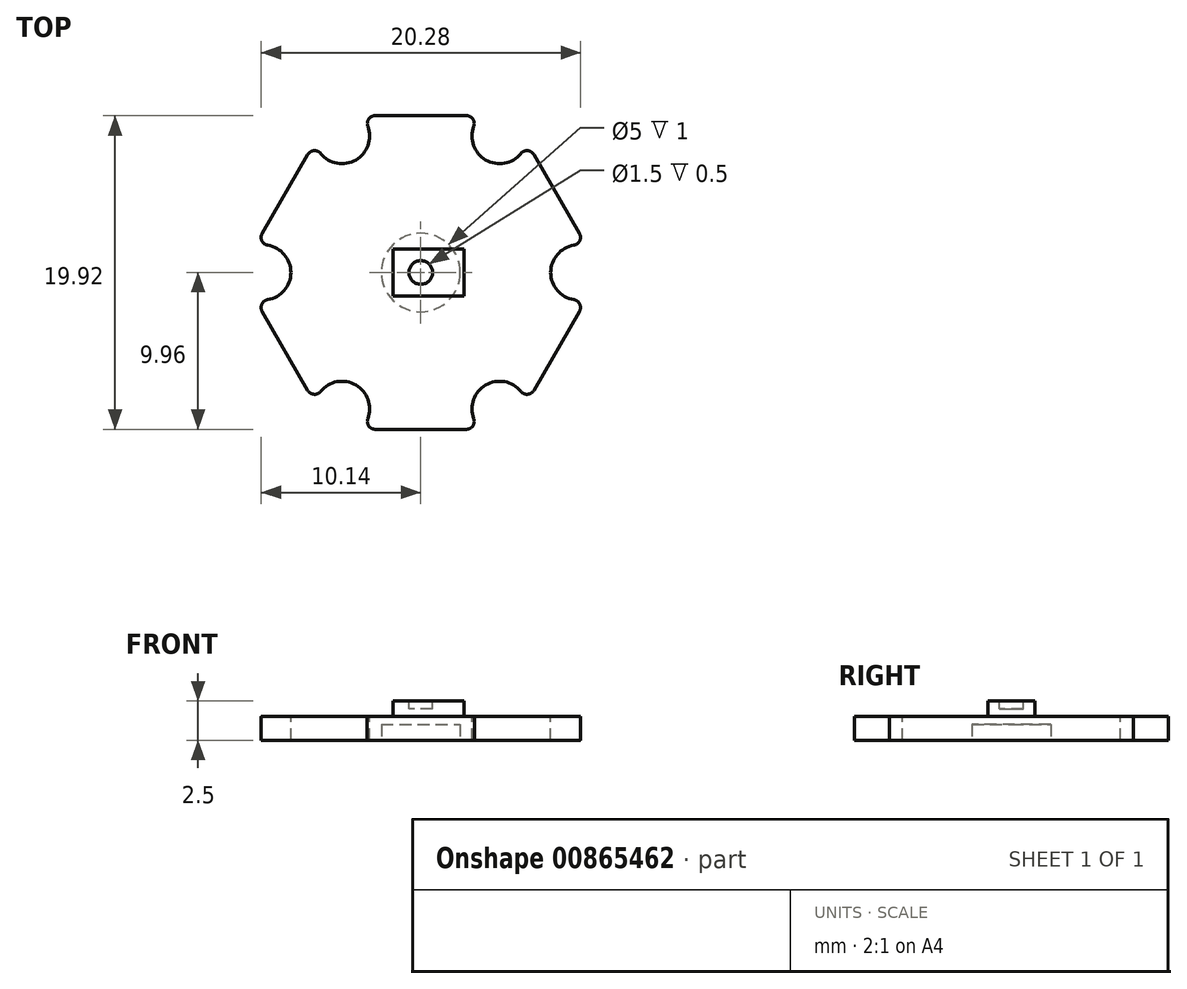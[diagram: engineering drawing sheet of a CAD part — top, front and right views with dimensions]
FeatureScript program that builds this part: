
annotation { "Feature Type Name" : "Feature", "Feature Type Description" : "" }
export const myFeature = defineFeature(function(context is Context, id is Id, definition is map)
    precondition{}
    {
        {
            var Q0;
            Q0=qCreatedBy(makeId("Top.planeOp"),FACE);
            var sketch = newSketch(context, id + "F0", { "sketchPlane" : qUnion([Q0])});
            skCircle(sketch, "E0.cCircle", {"center": v(0, 0) * mm, "radius": 9.96 * mm, "construction": true});
            skLineSegment(sketch, "E0.0", {"start": v(-5.75, 9.96) * mm, "end": v(5.75, 9.96) * mm});
            skLineSegment(sketch, "E0.1", {"start": v(5.75, 9.96) * mm, "end": v(11.5, 0) * mm});
            skLineSegment(sketch, "E0.2", {"start": v(11.5, 0) * mm, "end": v(5.75, -9.96) * mm});
            skLineSegment(sketch, "E0.3", {"start": v(5.75, -9.96) * mm, "end": v(-5.75, -9.96) * mm});
            skLineSegment(sketch, "E0.4", {"start": v(-5.75, -9.96) * mm, "end": v(-11.5, 0) * mm});
            skLineSegment(sketch, "E0.5", {"start": v(-11.5, 0) * mm, "end": v(-5.75, 9.96) * mm});
            skPoint(sketch, "E0.0.midPoint", {"position": v(0, 9.96) * mm});
            skSolve(sketch);
        }
        {
            var Q0;
            Q0 = qSketchRegion(id + "F0", true);
            extrude(context, id + "F1", {"entities" : qUnion([Q0]), "depth" : 1.5 * mm, "offsetDistance" : 25 * mm});
        }
        {
            var Q0;
            Q0=makeQuery(id+"F1.opExtrude","CAP_FACE",FACE,{"disambiguationData":[OSD([sQuery(id+"F0.wireOp",EDGE,"E0.0"),sQuery(id+"F0.wireOp",EDGE,"E0.1"),sQuery(id+"F0.wireOp",EDGE,"E0.2"),sQuery(id+"F0.wireOp",EDGE,"E0.3"),sQuery(id+"F0.wireOp",EDGE,"E0.4"),sQuery(id+"F0.wireOp",EDGE,"E0.5")])],"isStart":false});
            var sketch = newSketch(context, id + "F2", { "sketchPlane" : qUnion([Q0])});
            skLineSegment(sketch, "E1", {"start": v(-5.75, 9.96) * mm, "end": v(5.75, -9.96) * mm});
            skCircle(sketch, "E2", {"center": v(-5, 8.66) * mm, "radius": 1.75 * mm});
            skCircle(sketch, "E3", {"center": v(5, -8.66) * mm, "radius": 1.75 * mm});
            skLineSegment(sketch, "E4", {"start": v(5.75, 9.96) * mm, "end": v(-5.75, -9.96) * mm});
            skLineSegment(sketch, "E5", {"start": v(-11.5, 0) * mm, "end": v(11.5, 0) * mm});
            skCircle(sketch, "E6", {"center": v(5, 8.66) * mm, "radius": 1.75 * mm});
            skCircle(sketch, "E7", {"center": v(-5, -8.66) * mm, "radius": 1.75 * mm});
            skCircle(sketch, "E8", {"center": v(10, 0) * mm, "radius": 1.75 * mm});
            skCircle(sketch, "E9", {"center": v(-10, 0) * mm, "radius": 1.75 * mm});
            skSolve(sketch);
        }
        {
            var Q0;
            Q0 = qSketchRegion(id + "F2", true);
            extrude(context, id + "F3", {"entities" : qUnion([Q0]), "operationType" : NewBodyOperationType.REMOVE, "oppositeDirection" : true, "depth" : 25 * mm, "offsetDistance" : 25 * mm});
        }
        {
            var Q0;
            Q0=makeQuery(id+"F3.boolean.opBoolean","INTERSECT",EDGE,{"derivedFrom":[makeQuery(id+"F1.opExtrude","SWEPT_FACE",FACE,{"disambiguationData":[OSD([sQuery(id+"F0.wireOp",EDGE,"E0.0")])]}),makeQuery(id+"F3.opExtrude","SWEPT_FACE",FACE,{"disambiguationData":[OSD([sQuery(id+"F2.wireOp",EDGE,"E2")])]})]});
            var Q1;
            Q1=makeQuery(id+"F3.boolean.opBoolean","INTERSECT",EDGE,{"derivedFrom":[makeQuery(id+"F1.opExtrude","SWEPT_FACE",FACE,{"disambiguationData":[OSD([sQuery(id+"F0.wireOp",EDGE,"E0.5")])]}),makeQuery(id+"F3.opExtrude","SWEPT_FACE",FACE,{"disambiguationData":[OSD([sQuery(id+"F2.wireOp",EDGE,"E2")])]})]});
            var Q2;
            Q2=makeQuery(id+"F3.boolean.opBoolean","INTERSECT",EDGE,{"derivedFrom":[makeQuery(id+"F1.opExtrude","SWEPT_FACE",FACE,{"disambiguationData":[OSD([sQuery(id+"F0.wireOp",EDGE,"E0.0")])]}),makeQuery(id+"F3.opExtrude","SWEPT_FACE",FACE,{"disambiguationData":[OSD([sQuery(id+"F2.wireOp",EDGE,"E6")])]})]});
            var Q3;
            Q3=makeQuery(id+"F3.boolean.opBoolean","INTERSECT",EDGE,{"derivedFrom":[makeQuery(id+"F1.opExtrude","SWEPT_FACE",FACE,{"disambiguationData":[OSD([sQuery(id+"F0.wireOp",EDGE,"E0.1")])]}),makeQuery(id+"F3.opExtrude","SWEPT_FACE",FACE,{"disambiguationData":[OSD([sQuery(id+"F2.wireOp",EDGE,"E6")])]})]});
            var Q4;
            Q4=makeQuery(id+"F3.boolean.opBoolean","INTERSECT",EDGE,{"derivedFrom":[makeQuery(id+"F1.opExtrude","SWEPT_FACE",FACE,{"disambiguationData":[OSD([sQuery(id+"F0.wireOp",EDGE,"E0.5")])]}),makeQuery(id+"F3.opExtrude","SWEPT_FACE",FACE,{"disambiguationData":[OSD([sQuery(id+"F2.wireOp",EDGE,"E9")])]})]});
            var Q5;
            Q5=makeQuery(id+"F3.boolean.opBoolean","INTERSECT",EDGE,{"derivedFrom":[makeQuery(id+"F1.opExtrude","SWEPT_FACE",FACE,{"disambiguationData":[OSD([sQuery(id+"F0.wireOp",EDGE,"E0.4")])]}),makeQuery(id+"F3.opExtrude","SWEPT_FACE",FACE,{"disambiguationData":[OSD([sQuery(id+"F2.wireOp",EDGE,"E9")])]})]});
            var Q6;
            Q6=makeQuery(id+"F3.boolean.opBoolean","INTERSECT",EDGE,{"derivedFrom":[makeQuery(id+"F1.opExtrude","SWEPT_FACE",FACE,{"disambiguationData":[OSD([sQuery(id+"F0.wireOp",EDGE,"E0.3")])]}),makeQuery(id+"F3.opExtrude","SWEPT_FACE",FACE,{"disambiguationData":[OSD([sQuery(id+"F2.wireOp",EDGE,"E7")])]})]});
            var Q7;
            Q7=makeQuery(id+"F3.boolean.opBoolean","INTERSECT",EDGE,{"derivedFrom":[makeQuery(id+"F1.opExtrude","SWEPT_FACE",FACE,{"disambiguationData":[OSD([sQuery(id+"F0.wireOp",EDGE,"E0.4")])]}),makeQuery(id+"F3.opExtrude","SWEPT_FACE",FACE,{"disambiguationData":[OSD([sQuery(id+"F2.wireOp",EDGE,"E7")])]})]});
            var Q8;
            Q8=makeQuery(id+"F3.boolean.opBoolean","INTERSECT",EDGE,{"derivedFrom":[makeQuery(id+"F1.opExtrude","SWEPT_FACE",FACE,{"disambiguationData":[OSD([sQuery(id+"F0.wireOp",EDGE,"E0.3")])]}),makeQuery(id+"F3.opExtrude","SWEPT_FACE",FACE,{"disambiguationData":[OSD([sQuery(id+"F2.wireOp",EDGE,"E3")])]})]});
            var Q9;
            Q9=makeQuery(id+"F3.boolean.opBoolean","INTERSECT",EDGE,{"derivedFrom":[makeQuery(id+"F1.opExtrude","SWEPT_FACE",FACE,{"disambiguationData":[OSD([sQuery(id+"F0.wireOp",EDGE,"E0.2")])]}),makeQuery(id+"F3.opExtrude","SWEPT_FACE",FACE,{"disambiguationData":[OSD([sQuery(id+"F2.wireOp",EDGE,"E3")])]})]});
            var Q10;
            Q10=makeQuery(id+"F3.boolean.opBoolean","INTERSECT",EDGE,{"derivedFrom":[makeQuery(id+"F1.opExtrude","SWEPT_FACE",FACE,{"disambiguationData":[OSD([sQuery(id+"F0.wireOp",EDGE,"E0.1")])]}),makeQuery(id+"F3.opExtrude","SWEPT_FACE",FACE,{"disambiguationData":[OSD([sQuery(id+"F2.wireOp",EDGE,"E8")])]})]});
            var Q11;
            Q11=makeQuery(id+"F3.boolean.opBoolean","INTERSECT",EDGE,{"derivedFrom":[makeQuery(id+"F1.opExtrude","SWEPT_FACE",FACE,{"disambiguationData":[OSD([sQuery(id+"F0.wireOp",EDGE,"E0.2")])]}),makeQuery(id+"F3.opExtrude","SWEPT_FACE",FACE,{"disambiguationData":[OSD([sQuery(id+"F2.wireOp",EDGE,"E8")])]})]});
            fillet(context, id + "F4", {"entities" : qUnion([Q0, Q1, Q2, Q3, Q4, Q5, Q6, Q7, Q8, Q9, Q10, Q11]), "radius" : 0.5 * mm, "tangentPropagation" : true, "allowEdgeOverflow" : false});
        }
        {
            var Q0;
            Q0=makeQuery(id+"F1.opExtrude","CAP_FACE",FACE,{"disambiguationData":[OSD([sQuery(id+"F0.wireOp",EDGE,"E0.0"),sQuery(id+"F0.wireOp",EDGE,"E0.1"),sQuery(id+"F0.wireOp",EDGE,"E0.2"),sQuery(id+"F0.wireOp",EDGE,"E0.3"),sQuery(id+"F0.wireOp",EDGE,"E0.4"),sQuery(id+"F0.wireOp",EDGE,"E0.5")])],"isStart":true});
            var sketch = newSketch(context, id + "F5", { "sketchPlane" : qUnion([Q0])});
            skCircle(sketch, "E10", {"center": v(0, 0) * mm, "radius": 2.5 * mm});
            skSolve(sketch);
        }
        {
            var Q0;
            Q0 = qSketchRegion(id + "F5", true);
            extrude(context, id + "F6", {"entities" : qUnion([Q0]), "operationType" : NewBodyOperationType.REMOVE, "oppositeDirection" : true, "depth" : 1 * mm, "offsetDistance" : 25 * mm});
        }
        {
            var Q0;
            Q0=makeQuery(id+"F1.opExtrude","CAP_FACE",FACE,{"disambiguationData":[OSD([sQuery(id+"F0.wireOp",EDGE,"E0.0"),sQuery(id+"F0.wireOp",EDGE,"E0.1"),sQuery(id+"F0.wireOp",EDGE,"E0.2"),sQuery(id+"F0.wireOp",EDGE,"E0.3"),sQuery(id+"F0.wireOp",EDGE,"E0.4"),sQuery(id+"F0.wireOp",EDGE,"E0.5")])],"isStart":false});
            var sketch = newSketch(context, id + "F7", { "sketchPlane" : qUnion([Q0])});
            skLineSegment(sketch, "E11.bottom", {"start": v(-1.75, 1.5) * mm, "end": v(2.75, 1.5) * mm});
            skLineSegment(sketch, "E11.top", {"start": v(-1.75, -1.5) * mm, "end": v(2.75, -1.5) * mm});
            skLineSegment(sketch, "E11.left", {"start": v(-1.75, 1.5) * mm, "end": v(-1.75, -1.5) * mm});
            skLineSegment(sketch, "E11.right", {"start": v(2.75, 1.5) * mm, "end": v(2.75, -1.5) * mm});
            skSolve(sketch);
        }
        {
            var Q0;
            Q0 = qSketchRegion(id + "F7", true);
            extrude(context, id + "F8", {"entities" : qUnion([Q0]), "operationType" : NewBodyOperationType.ADD, "depth" : 1 * mm, "offsetDistance" : 25 * mm});
        }
        {
            var Q0;
            Q0=makeQuery(id+"F8.opExtrude","CAP_FACE",FACE,{"disambiguationData":[OSD([sQuery(id+"F7.wireOp",EDGE,"E11.bottom"),sQuery(id+"F7.wireOp",EDGE,"E11.top"),sQuery(id+"F7.wireOp",EDGE,"E11.left"),sQuery(id+"F7.wireOp",EDGE,"E11.right")])],"isStart":false});
            var sketch = newSketch(context, id + "F9", { "sketchPlane" : qUnion([Q0])});
            skCircle(sketch, "E12", {"center": v(0, 0) * mm, "radius": 0.75 * mm});
            skSolve(sketch);
        }
        {
            var Q0;
            Q0 = qSketchRegion(id + "F9", true);
            extrude(context, id + "F10", {"entities" : qUnion([Q0]), "operationType" : NewBodyOperationType.REMOVE, "oppositeDirection" : true, "depth" : 0.5 * mm, "offsetDistance" : 25 * mm});
        }
    });
